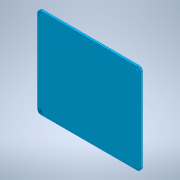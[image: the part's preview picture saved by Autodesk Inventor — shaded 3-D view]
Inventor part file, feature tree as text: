
AUTODESK INVENTOR PART (.ipt)
format: ipt  version: 2020 (Build 240168000, 168)  size: 128,512 bytes
history: native  units: mm
features: other x3, extrude x2, sketch x2, plane x1, reference x1, projected_geometry x1
ambient origin geometry x8: Origin, YZ Plane, XZ Plane, XY Plane, X Axis, Y Axis, Z Axis, Center Point
bodies: 实体1 (feature_tree)
feature tree (10):
  plane  "工作平面1"
  extrude  "拉伸1"  Depth=4.0mm
  extrude  "拉伸2"  Depth=4.0mm
  sketch  "草图1"  dims[d0=4.0mm d1=0.0mm d2=0.5mm]
  reference  "参考1"
  sketch  "草图2"  dims[d3=0.5mm d4=0.5mm d5=0.5mm d6=4.0mm d7=0.0mm]
  projected_geometry  "投影回路1"
  other  "<userpath>\Desktop\ME_course_project\课设试试\shaft_try_1.iam"
  other  "shaft_try_1.iam"
  other  "shang(1):1"
